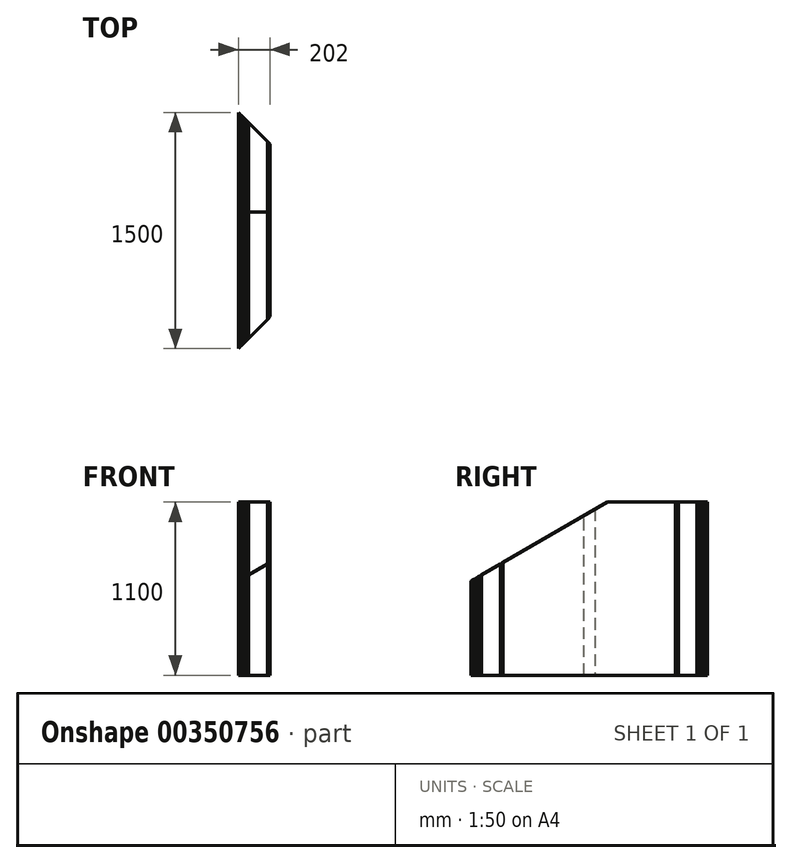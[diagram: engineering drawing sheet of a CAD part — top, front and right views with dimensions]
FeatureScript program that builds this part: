
annotation { "Feature Type Name" : "Feature", "Feature Type Description" : "" }
export const myFeature = defineFeature(function(context is Context, id is Id, definition is map)
    precondition{}
    {
        {
            var Q0;
            Q0=qCreatedBy(makeId("Right.planeOp"),FACE);
            var sketch = newSketch(context, id + "F0", { "sketchPlane" : qUnion([Q0])});
            skLineSegment(sketch, "E0", {"start": v(0, 0) * mm, "end": v(1500, 0) * mm});
            skLineSegment(sketch, "E1", {"start": v(1500, 0) * mm, "end": v(1500, 1100) * mm});
            skLineSegment(sketch, "E2", {"start": v(1500, 1100) * mm, "end": v(866.03, 1100) * mm});
            skLineSegment(sketch, "E3", {"start": v(866.03, 1100) * mm, "end": v(0, 600) * mm});
            skLineSegment(sketch, "E4", {"start": v(0, 600) * mm, "end": v(0, 0) * mm});
            skSolve(sketch);
        }
        {
            var Q0;
            Q0=makeQuery(id+"F0.imprint","IMPRINT",FACE,{"disambiguationData":[TD([[makeQuery(id+"F0.imprint","IMPRINT",EDGE,{"derivedFrom":sQuery(id+"F0.wireOp",EDGE,"E0")}),1.0]])]});
            extrude(context, id + "F1", {"entities" : qUnion([Q0]), "depth" : 6 * mm});
        }
        {
            var Q0;
            Q0=makeQuery(id+"F1.opExtrude","CAP_FACE",FACE,{"disambiguationData":[OSD([sQuery(id+"F0.wireOp",EDGE,"E0"),sQuery(id+"F0.wireOp",EDGE,"E1"),sQuery(id+"F0.wireOp",EDGE,"E2"),sQuery(id+"F0.wireOp",EDGE,"E3"),sQuery(id+"F0.wireOp",EDGE,"E4")])],"isStart":true});
            extrude(context, id + "F2", {"entities" : qUnion([Q0]), "depth" : 1 * mm});
        }
        {
            var Q0;
            Q0=makeQuery(id+"F2.opExtrude","CAP_FACE",FACE,{"disambiguationData":[OSD([sQuery(id+"F0.wireOp",EDGE,"E0"),sQuery(id+"F0.wireOp",EDGE,"E1"),sQuery(id+"F0.wireOp",EDGE,"E2"),sQuery(id+"F0.wireOp",EDGE,"E3"),sQuery(id+"F0.wireOp",EDGE,"E4")])],"isStart":false});
            extrude(context, id + "F3", {"entities" : qUnion([Q0]), "depth" : 10 * mm});
        }
        {
            var Q0;
            Q0=makeQuery(id+"F3.opExtrude","CAP_FACE",FACE,{"disambiguationData":[OSD([sQuery(id+"F0.wireOp",EDGE,"E0"),sQuery(id+"F0.wireOp",EDGE,"E1"),sQuery(id+"F0.wireOp",EDGE,"E2"),sQuery(id+"F0.wireOp",EDGE,"E3"),sQuery(id+"F0.wireOp",EDGE,"E4")])],"isStart":false});
            extrude(context, id + "F4", {"entities" : qUnion([Q0]), "depth" : 120 * mm});
        }
        {
            var Q0;
            Q0=makeQuery(id+"F4.opExtrude","CAP_FACE",FACE,{"disambiguationData":[OSD([sQuery(id+"F0.wireOp",EDGE,"E0"),sQuery(id+"F0.wireOp",EDGE,"E1"),sQuery(id+"F0.wireOp",EDGE,"E2"),sQuery(id+"F0.wireOp",EDGE,"E3"),sQuery(id+"F0.wireOp",EDGE,"E4")])],"isStart":false});
            extrude(context, id + "F5", {"entities" : qUnion([Q0]), "depth" : 10 * mm});
        }
        {
            var Q0;
            Q0=makeQuery(id+"F5.opExtrude","CAP_FACE",FACE,{"disambiguationData":[OSD([sQuery(id+"F0.wireOp",EDGE,"E0"),sQuery(id+"F0.wireOp",EDGE,"E1"),sQuery(id+"F0.wireOp",EDGE,"E2"),sQuery(id+"F0.wireOp",EDGE,"E3"),sQuery(id+"F0.wireOp",EDGE,"E4")])],"isStart":false});
            extrude(context, id + "F6", {"entities" : qUnion([Q0]), "depth" : 10 * mm});
        }
        {
            var Q0;
            Q0=makeQuery(id+"F6.opExtrude","CAP_FACE",FACE,{"disambiguationData":[OSD([sQuery(id+"F0.wireOp",EDGE,"E0"),sQuery(id+"F0.wireOp",EDGE,"E1"),sQuery(id+"F0.wireOp",EDGE,"E2"),sQuery(id+"F0.wireOp",EDGE,"E3"),sQuery(id+"F0.wireOp",EDGE,"E4")])],"isStart":false});
            extrude(context, id + "F7", {"entities" : qUnion([Q0]), "depth" : 18 * mm});
        }
        {
            var Q0;
            Q0=makeQuery(id+"F7.opExtrude","CAP_FACE",FACE,{"disambiguationData":[OSD([sQuery(id+"F0.wireOp",EDGE,"E0"),sQuery(id+"F0.wireOp",EDGE,"E1"),sQuery(id+"F0.wireOp",EDGE,"E2"),sQuery(id+"F0.wireOp",EDGE,"E3"),sQuery(id+"F0.wireOp",EDGE,"E4")])],"isStart":false});
            extrude(context, id + "F8", {"entities" : qUnion([Q0]), "depth" : 10 * mm});
        }
        {
            var Q0;
            Q0=makeQuery(id+"F8.opExtrude","CAP_FACE",FACE,{"disambiguationData":[OSD([sQuery(id+"F0.wireOp",EDGE,"E0"),sQuery(id+"F0.wireOp",EDGE,"E1"),sQuery(id+"F0.wireOp",EDGE,"E2"),sQuery(id+"F0.wireOp",EDGE,"E3"),sQuery(id+"F0.wireOp",EDGE,"E4")])],"isStart":false});
            extrude(context, id + "F9", {"entities" : qUnion([Q0]), "depth" : 1 * mm});
        }
        {
            var Q0;
            Q0=makeQuery(id+"F9.opExtrude","CAP_FACE",FACE,{"disambiguationData":[OSD([sQuery(id+"F0.wireOp",EDGE,"E0"),sQuery(id+"F0.wireOp",EDGE,"E1"),sQuery(id+"F0.wireOp",EDGE,"E2"),sQuery(id+"F0.wireOp",EDGE,"E3"),sQuery(id+"F0.wireOp",EDGE,"E4")])],"isStart":false});
            var sketch = newSketch(context, id + "F10", { "sketchPlane" : qUnion([Q0])});
            skLineSegment(sketch, "E5.bottom", {"start": v(-1500, 0) * mm, "end": v(-1430, 0) * mm});
            skLineSegment(sketch, "E5.top", {"start": v(-1500, 1100) * mm, "end": v(-1430, 1100) * mm});
            skLineSegment(sketch, "E5.left", {"start": v(-1500, 0) * mm, "end": v(-1500, 1100) * mm});
            skLineSegment(sketch, "E5.right", {"start": v(-1430, 0) * mm, "end": v(-1430, 1100) * mm});
            skLineSegment(sketch, "E6", {"start": v(0, 0) * mm, "end": v(0, 600) * mm});
            skLineSegment(sketch, "E7", {"start": v(0, 600) * mm, "end": v(-70, 640.41) * mm});
            skLineSegment(sketch, "E8", {"start": v(-70, 640.41) * mm, "end": v(-70, 0) * mm});
            skLineSegment(sketch, "E9", {"start": v(-70, 0) * mm, "end": v(0, 0) * mm});
            skLineSegment(sketch, "E10", {"start": v(-715, 0) * mm, "end": v(-715, 1012.8) * mm});
            skLineSegment(sketch, "E11", {"start": v(-715, 1012.8) * mm, "end": v(-785, 1053.22) * mm});
            skLineSegment(sketch, "E12", {"start": v(-785, 1053.22) * mm, "end": v(-785, 0) * mm});
            skLineSegment(sketch, "E13", {"start": v(-785, 0) * mm, "end": v(-715, 0) * mm});
            skLineSegment(sketch, "E14", {"start": v(-1430, 0) * mm, "end": v(-785, 0) * mm, "construction": true});
            skLineSegment(sketch, "E15", {"start": v(-715, 0) * mm, "end": v(-70, 0) * mm, "construction": true});
            skSolve(sketch);
        }
        {
            var Q0;
            Q0=makeQuery(id+"F10.imprint","IMPRINT",FACE,{"disambiguationData":[TD([[makeQuery(id+"F10.imprint","IMPRINT",EDGE,{"derivedFrom":sQuery(id+"F10.wireOp",EDGE,"E5.bottom")}),-1.0]])]});
            var Q1;
            Q1=makeQuery(id+"F10.imprint","IMPRINT",FACE,{"disambiguationData":[TD([[makeQuery(id+"F10.imprint","IMPRINT",EDGE,{"derivedFrom":sQuery(id+"F10.wireOp",EDGE,"E10")}),1.0]])]});
            var Q2;
            Q2=makeQuery(id+"F10.imprint","IMPRINT",FACE,{"disambiguationData":[TD([[makeQuery(id+"F10.imprint","IMPRINT",EDGE,{"derivedFrom":sQuery(id+"F10.wireOp",EDGE,"E6")}),-1.0]])]});
            extrude(context, id + "F11", {"entities" : qUnion([Q0, Q1, Q2]), "depth" : 8 * mm});
        }
        {
            var Q0;
            Q0=makeQuery(id+"F11.opExtrude","CAP_FACE",FACE,{"disambiguationData":[OSD([sQuery(id+"F10.wireOp",EDGE,"E10"),sQuery(id+"F10.wireOp",EDGE,"E11"),sQuery(id+"F10.wireOp",EDGE,"E12"),sQuery(id+"F10.wireOp",EDGE,"E13")])],"isStart":false});
            var sketch = newSketch(context, id + "F12", { "sketchPlane" : qUnion([Q0])});
            skLineSegment(sketch, "E16", {"start": v(-1500, 1100) * mm, "end": v(-866.03, 1100) * mm});
            skLineSegment(sketch, "E17", {"start": v(-866.03, 1100) * mm, "end": v(0, 600) * mm});
            skLineSegment(sketch, "E18", {"start": v(0, 600) * mm, "end": v(0, 0) * mm});
            skLineSegment(sketch, "E19", {"start": v(0, 0) * mm, "end": v(-1500, 0) * mm});
            skLineSegment(sketch, "E20", {"start": v(-1500, 0) * mm, "end": v(-1500, 1100) * mm});
            skSolve(sketch);
        }
        {
            var Q0;
            Q0 = qSketchRegion(id + "F12", true);
            extrude(context, id + "F13", {"entities" : qUnion([Q0]), "depth" : 8 * mm});
        }
        {
            var Q0;
            Q0=makeQuery(id+"F4.opExtrude","SWEPT_FACE",FACE,{"disambiguationData":[OSD([sQuery(id+"F0.wireOp",EDGE,"E2")])]});
            var sketch = newSketch(context, id + "F14", { "sketchPlane" : qUnion([Q0])});
            skLineSegment(sketch, "E21", {"start": v(-196, 1500) * mm, "end": v(6, 1298) * mm});
            skLineSegment(sketch, "E22", {"start": v(6, 1298) * mm, "end": v(6, 1500) * mm});
            skLineSegment(sketch, "E23", {"start": v(6, 1500) * mm, "end": v(-196, 1500) * mm});
            skSolve(sketch);
        }
        {
            var Q0;
            Q0 = qSketchRegion(id + "F14", true);
            extrude(context, id + "F15", {"entities" : qUnion([Q0]), "operationType" : NewBodyOperationType.REMOVE, "endBound" : BoundingType.THROUGH_ALL, "oppositeDirection" : true, "depth" : 25 * mm});
        }
        {
            var Q0;
            Q0=makeQuery(id+"F4.opExtrude","SWEPT_FACE",FACE,{"disambiguationData":[OSD([sQuery(id+"F0.wireOp",EDGE,"E0")])]});
            var sketch = newSketch(context, id + "F16", { "sketchPlane" : qUnion([Q0])});
            skLineSegment(sketch, "E24", {"start": v(-196, 0) * mm, "end": v(6, -202) * mm});
            skLineSegment(sketch, "E25", {"start": v(6, -202) * mm, "end": v(6, 0) * mm});
            skLineSegment(sketch, "E26", {"start": v(6, 0) * mm, "end": v(-196, 0) * mm});
            skSolve(sketch);
        }
        {
            var Q0;
            Q0 = qSketchRegion(id + "F16", true);
            extrude(context, id + "F17", {"entities" : qUnion([Q0]), "operationType" : NewBodyOperationType.REMOVE, "endBound" : BoundingType.THROUGH_ALL, "oppositeDirection" : true, "depth" : 25 * mm});
        }
    });
